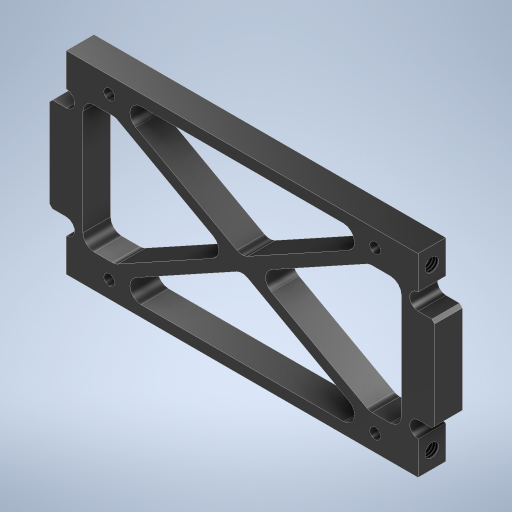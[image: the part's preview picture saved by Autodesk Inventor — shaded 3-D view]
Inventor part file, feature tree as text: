
AUTODESK INVENTOR PART (.ipt)
format: ipt  version: 2024.2 (Build 282272000, 272)  size: 366,592 bytes
history: native  units: mm
features: sketch x2, hole x2, extrude x1, mirror x1, chamfer x1
ambient origin geometry x8: Origin, YZ Plane, XZ Plane, XY Plane, X Axis, Y Axis, Z Axis, Center Point
bodies: Solid1 (feature_tree)
feature tree (7):
  sketch  "Sketch1"  dims[d0=63.5mm d1=35.0mm]
  extrude  "Extrusion1"  Depth=35.0mm
  hole  "Hole1"  [1 undecoded]
  mirror  "Mirror1"
  chamfer  "Chamfer1"  Distance=3.0mm
  hole  "Hole2"  [1 undecoded]
  sketch  "Sketch2"  dims[d2=1.5mm d3=6.0mm d4=3.0mm d5=6.0mm d6=2.0mm d7=2.0mm d9=2.0mm d10=3.0mm d11=3.0mm d12=5.0mm d13=0.0mm d14=2.459mm d15=6.0mm d16=4.0mm d17=2.0mm d18=90.0deg d19=6.0mm d20=0.0mm d21=0.5mm d22=2.0mm d23=45.0deg d24=48.0mm d25=2.0mm d26=6.0mm d27=4.0mm d28=2.0mm d29=90.0deg d30=8.0mm d31=20.594885mm]
note: 2 required parameter values undecoded (feature->parameter linkage not recoverable at this tier; creation-order binding heuristic only, values carry confidence <= 0.55)
